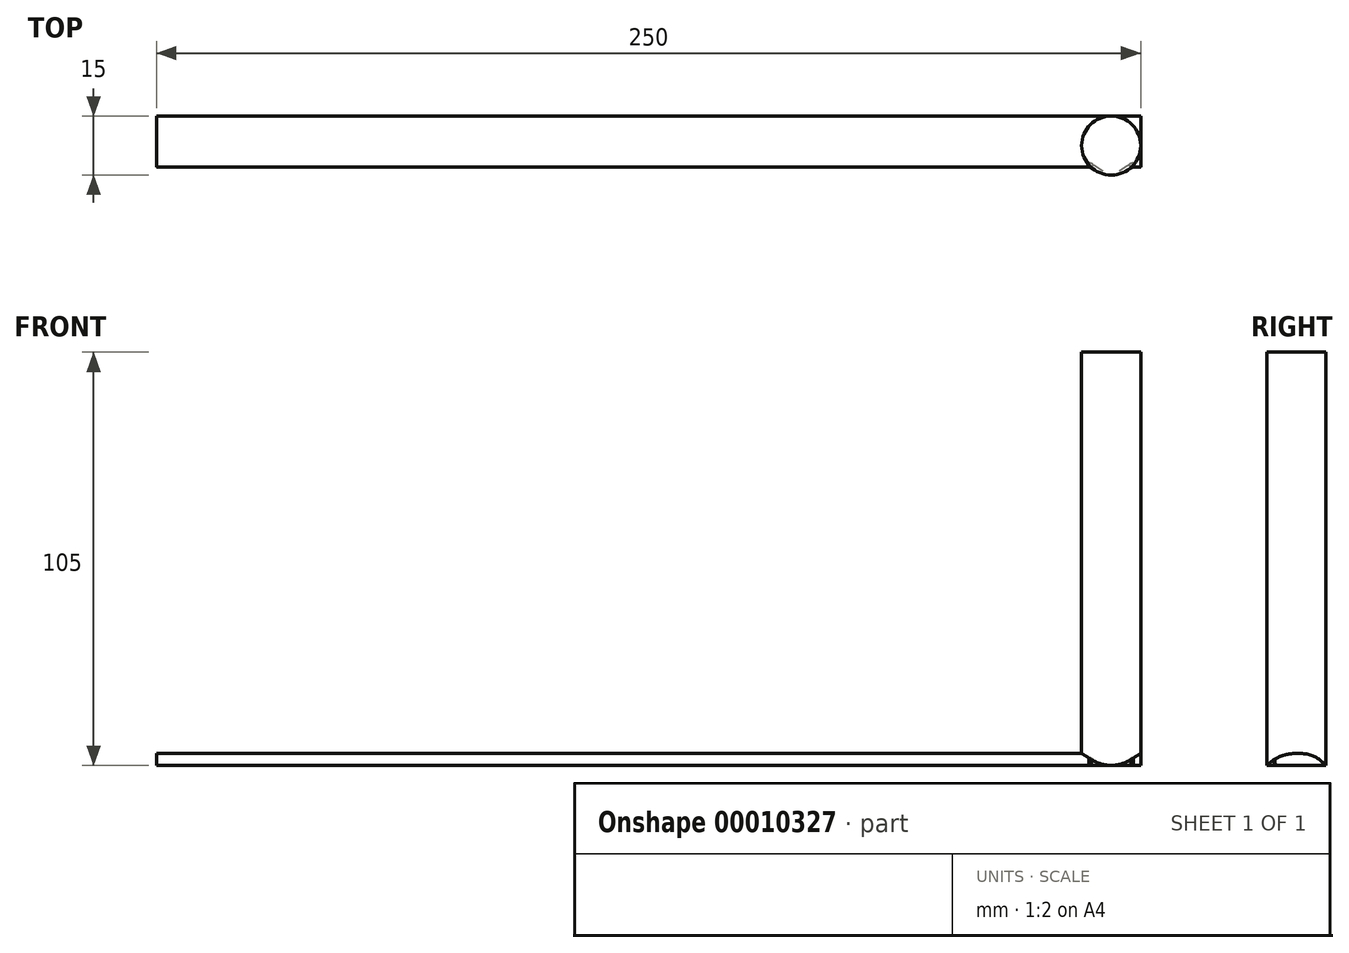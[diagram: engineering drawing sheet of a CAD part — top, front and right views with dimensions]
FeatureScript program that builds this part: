
annotation { "Feature Type Name" : "Feature", "Feature Type Description" : "" }
export const myFeature = defineFeature(function(context is Context, id is Id, definition is map)
    precondition{}
    {
        {
            var Q0;
            Q0=qCreatedBy(makeId("Right.planeOp"),FACE);
            var sketch = newSketch(context, id + "F0", { "sketchPlane" : qUnion([Q0])});
            skLineSegment(sketch, "E0", {"start": v(0, 0) * mm, "end": v(15, 0) * mm});
            skFitSpline(sketch, "E1", {"points": [v(0, 0) * mm, v(3.21, 2.2) * mm, v(7.7, 3.08) * mm, v(12.1, 2.29) * mm, v(15, 0) * mm], "startDerivative": vector(12.35, 10.24) * mm, "endDerivative": vector(11.2, -11.06) * mm});
            skSolve(sketch);
        }
        {
            var Q0;
            Q0 = qSketchRegion(id + "F0", true);
            extrude(context, id + "F1", {"entities" : qUnion([Q0]), "depth" : 250 * mm});
        }
        {
            var Q0;
            Q0=makeQuery(id+"F1.opExtrude","SWEPT_FACE",FACE,{"disambiguationData":[OSD([sQuery(id+"F0.wireOp",EDGE,"E0")])]});
            var sketch = newSketch(context, id + "F2", { "sketchPlane" : qUnion([Q0])});
            skCircle(sketch, "E2", {"center": v(242.5, -7.5) * mm, "radius": 7.5 * mm});
            skSolve(sketch);
        }
        {
            var Q0;
            Q0 = qSketchRegion(id + "F2", true);
            extrude(context, id + "F3", {"entities" : qUnion([Q0]), "operationType" : NewBodyOperationType.ADD, "oppositeDirection" : true, "depth" : 105 * mm});
        }
        {
            var Q0;
            {var subQ0=sQuery(id+"F0.wireOp",EDGE,"E0");var subQ1=sQuery(id+"F0.wireOp",EDGE,"E1");Q0=makeQuery(id+"F3.boolean.opBoolean","SPLIT",EDGE,{"disambiguationData":[TD([makeQuery(id+"F1.opExtrude","CAP_FACE",FACE,{"disambiguationData":[OSD([subQ0,subQ1])],"isStart":true})])],"derivedFrom":makeQuery(id+"F1.opExtrude","SWEPT_EDGE",EDGE,{"disambiguationData":[OSD([subQ0,subQ1]),TDD([makeQuery(id+"F0.imprint","INTERSECT",VERTEX,{"disambiguationData":[OD(0.0)],"derivedFrom":[subQ0,subQ1]})])]})});}
            fillet(context, id + "F4", {"entities" : qUnion([Q0]), "radius" : 1 * mm, "tangentPropagation" : true, "allowEdgeOverflow" : false});
        }
    });
